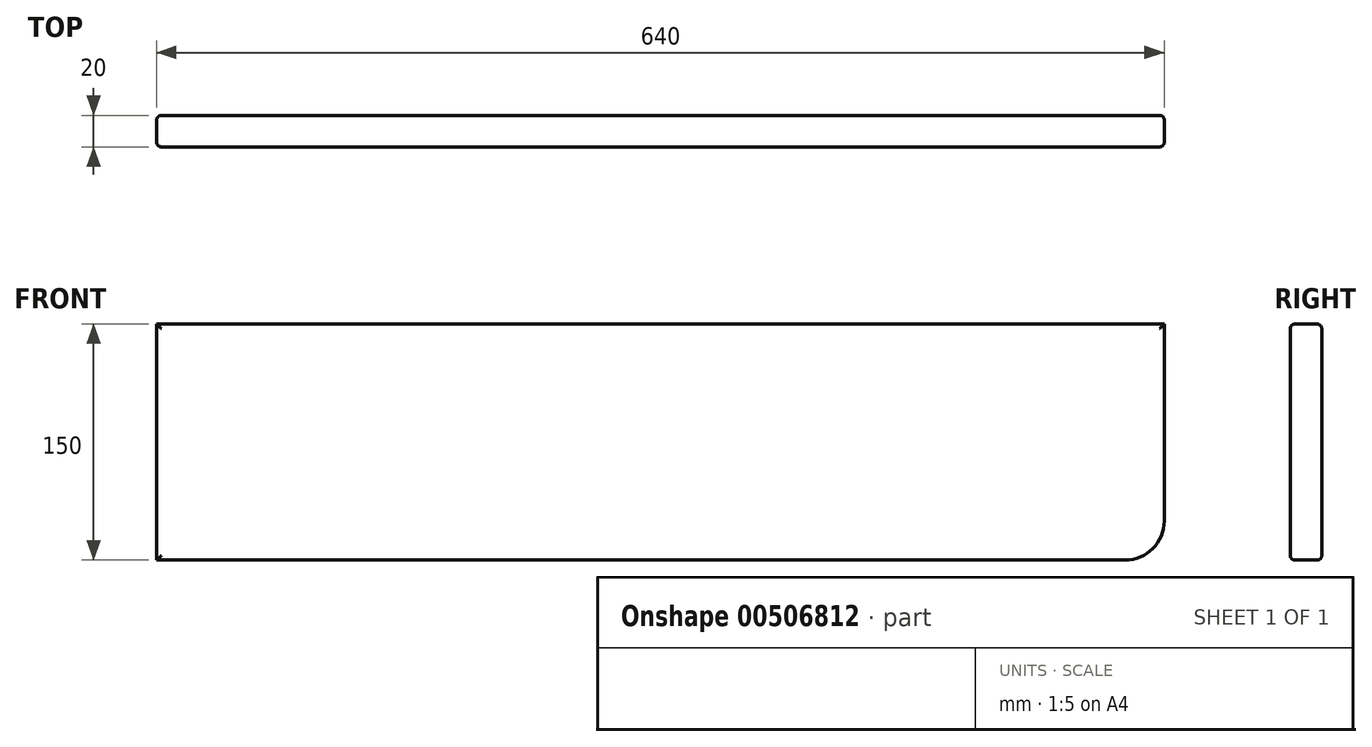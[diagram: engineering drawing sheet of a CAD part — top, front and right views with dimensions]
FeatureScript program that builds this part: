
annotation { "Feature Type Name" : "Feature", "Feature Type Description" : "" }
export const myFeature = defineFeature(function(context is Context, id is Id, definition is map)
    precondition{}
    {
        {
            var Q0;
            Q0=qCreatedBy(makeId("Front.planeOp"),FACE);
            var sketch = newSketch(context, id + "F0", { "sketchPlane" : qUnion([Q0])});
            skLineSegment(sketch, "E0.bottom", {"start": v(-390.07, -20.82) * mm, "end": v(249.93, -20.82) * mm});
            skLineSegment(sketch, "E0.top", {"start": v(-390.07, -170.82) * mm, "end": v(224.93, -170.82) * mm});
            skLineSegment(sketch, "E0.left", {"start": v(-390.07, -20.82) * mm, "end": v(-390.07, -170.82) * mm});
            skLineSegment(sketch, "E0.right", {"start": v(249.93, -20.82) * mm, "end": v(249.93, -145.82) * mm});
            skPoint(sketch, "E1.visualSharp", {"position": v(249.93, -170.82) * mm});
            skArc(sketch, "E1.filletArc", {"start": v(224.93, -170.82) * mm, "mid": v(242.6, -163.5) * mm, "end": v(249.93, -145.82) * mm});
            skSolve(sketch);
        }
        {
            var Q0;
            Q0=makeQuery(id+"F0.imprint","IMPRINT",FACE,{"disambiguationData":[TD([[makeQuery(id+"F0.imprint","IMPRINT",EDGE,{"derivedFrom":sQuery(id+"F0.wireOp",EDGE,"E0.bottom")}),-1.0]])]});
            extrude(context, id + "F1", {"entities" : qUnion([Q0]), "depth" : 20 * mm});
        }
        {
            var Q0;
            Q0=makeQuery(id+"F1.opExtrude","CAP_FACE",FACE,{"disambiguationData":[OSD([sQuery(id+"F0.wireOp",EDGE,"E0.bottom"),sQuery(id+"F0.wireOp",EDGE,"E0.top"),sQuery(id+"F0.wireOp",EDGE,"E0.left"),sQuery(id+"F0.wireOp",EDGE,"E0.right")])],"isStart":true});
            var sketch = newSketch(context, id + "F2", { "sketchPlane" : qUnion([Q0])});
            skLineSegment(sketch, "E2", {"start": v(390.07, -170.82) * mm, "end": v(390.07, -50.82) * mm});
            skLineSegment(sketch, "E3", {"start": v(390.07, -50.82) * mm, "end": v(375.07, -50.82) * mm});
            skLineSegment(sketch, "E4", {"start": v(-194.93, -50.82) * mm, "end": v(-249.93, -50.82) * mm});
            skLineSegment(sketch, "E5", {"start": v(375.07, -50.82) * mm, "end": v(-194.93, -50.82) * mm});
            skLineSegment(sketch, "E6", {"start": v(378.5, -20.82) * mm, "end": v(378.5, -50.82) * mm});
            skSolve(sketch);
        }
        {
            var Q0;
            Q0=makeQuery(id+"F1.opExtrude","CAP_FACE",FACE,{"disambiguationData":[OSD([sQuery(id+"F0.wireOp",EDGE,"E0.bottom"),sQuery(id+"F0.wireOp",EDGE,"E0.top"),sQuery(id+"F0.wireOp",EDGE,"E0.left"),sQuery(id+"F0.wireOp",EDGE,"E0.right")])],"isStart":true});
            var Q1;
            Q1=makeQuery(id+"F1.opExtrude","CAP_FACE",FACE,{"disambiguationData":[OSD([sQuery(id+"F0.wireOp",EDGE,"E0.bottom"),sQuery(id+"F0.wireOp",EDGE,"E0.top"),sQuery(id+"F0.wireOp",EDGE,"E0.left"),sQuery(id+"F0.wireOp",EDGE,"E0.right")])],"isStart":false});
            fillet(context, id + "F3", {"entities" : qUnion([Q0, Q1]), "radius" : 3 * mm, "tangentPropagation" : true, "allowEdgeOverflow" : false});
        }
    });
